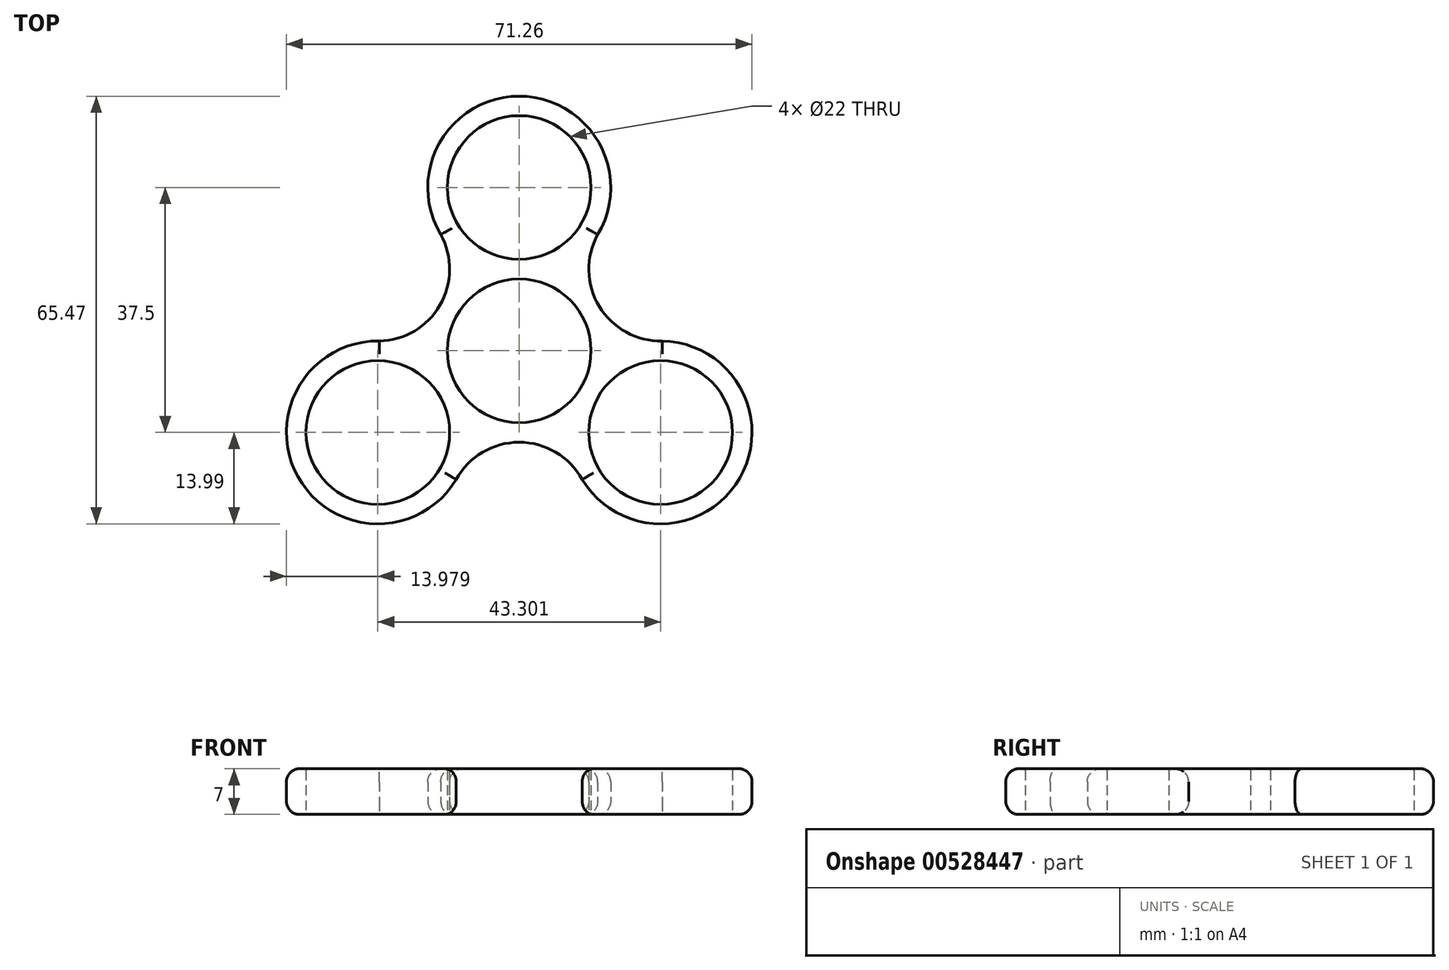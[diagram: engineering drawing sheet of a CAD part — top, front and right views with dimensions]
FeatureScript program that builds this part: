
annotation { "Feature Type Name" : "Feature", "Feature Type Description" : "" }
export const myFeature = defineFeature(function(context is Context, id is Id, definition is map)
    precondition{}
    {
        {
            var Q0;
            Q0=qCreatedBy(makeId("Top.planeOp"),FACE);
            var sketch = newSketch(context, id + "F0", { "sketchPlane" : qUnion([Q0])});
            skCircle(sketch, "E0", {"center": v(0, 0) * mm, "radius": 39 * mm, "construction": true});
            skCircle(sketch, "E1", {"center": v(0, 0) * mm, "radius": 11 * mm});
            skLineSegment(sketch, "E2", {"start": v(0, 39) * mm, "end": v(0, -39) * mm, "construction": true});
            skLineSegment(sketch, "E3", {"start": v(-39, 0) * mm, "end": v(39, 0) * mm, "construction": true});
            skCircle(sketch, "E4", {"center": v(0, 0) * mm, "radius": 25 * mm, "construction": true});
            skCircle(sketch, "E5", {"center": v(0, 25) * mm, "radius": 11 * mm});
            skCircle(sketch, "E6.1.0", {"center": v(-21.65, -12.5) * mm, "radius": 11 * mm});
            skCircle(sketch, "E6.2.0", {"center": v(21.65, -12.5) * mm, "radius": 11 * mm});
            skCircle(sketch, "E7", {"center": v(0, -25) * mm, "radius": 11 * mm, "construction": true});
            skCircle(sketch, "E8.1.0", {"center": v(21.65, 12.5) * mm, "radius": 11 * mm, "construction": true});
            skCircle(sketch, "E8.2.0", {"center": v(-21.65, 12.5) * mm, "radius": 11 * mm, "construction": true});
            skArc(sketch, "E9", {"start": v(-24.92, -2) * mm, "mid": v(-13.03, 7.52) * mm, "end": v(-10.73, 22.58) * mm, "construction": true});
            skArc(sketch, "E10.1.0", {"start": v(14.19, -20.58) * mm, "mid": v(0, -15.05) * mm, "end": v(-14.19, -20.58) * mm, "construction": true});
            skArc(sketch, "E10.2.0", {"start": v(10.73, 22.58) * mm, "mid": v(13.03, 7.52) * mm, "end": v(24.92, -2) * mm, "construction": true});
            skArc(sketch, "E11", {"start": v(-24.92, -2) * mm, "mid": v(-31.16, -18) * mm, "end": v(-14.19, -20.58) * mm, "construction": true});
            skArc(sketch, "E12", {"start": v(14.19, -20.58) * mm, "mid": v(31.16, -18) * mm, "end": v(24.92, -2) * mm, "construction": true});
            skArc(sketch, "E13", {"start": v(10.73, 22.58) * mm, "mid": v(0, 35.98) * mm, "end": v(-10.73, 22.58) * mm});
            skArc(sketch, "E14.2", {"start": v(-21.4, 1.5) * mm, "mid": v(-33.87, -19.28) * mm, "end": v(-9.64, -19.7) * mm});
            skArc(sketch, "E14.3", {"start": v(12, 17.79) * mm, "mid": v(0, 38.98) * mm, "end": v(-12, 17.79) * mm});
            skArc(sketch, "E14.5", {"start": v(9.4, -19.3) * mm, "mid": v(33.64, -19.7) * mm, "end": v(21.88, 1.5) * mm});
            skArc(sketch, "E15", {"start": v(-21.4, 1.5) * mm, "mid": v(-12.12, 7) * mm, "end": v(-12, 17.79) * mm});
            skArc(sketch, "E16", {"start": v(-9.64, -19.7) * mm, "mid": v(0, -14) * mm, "end": v(9.64, -19.7) * mm});
            skArc(sketch, "E17", {"start": v(21.88, 1.5) * mm, "mid": v(12.25, 6.8) * mm, "end": v(12, 17.79) * mm});
            skSolve(sketch);
        }
        {
            var Q0;
            Q0=makeQuery(id+"F0.imprint","IMPRINT",FACE,{"disambiguationData":[TD([[makeQuery(id+"F0.imprint","IMPRINT",EDGE,{"derivedFrom":sQuery(id+"F0.wireOp",EDGE,"E1")}),-1.0]])]});
            extrude(context, id + "F1", {"entities" : qUnion([Q0]), "depth" : 7 * mm, "offsetDistance" : 25 * mm});
        }
        {
            var Q0;
            Q0=makeQuery(id+"F1.opExtrude","CAP_EDGE",EDGE,{"disambiguationData":[OSD([sQuery(id+"F0.wireOp",EDGE,"E16")])],"isStart":false});
            var Q1;
            Q1=makeQuery(id+"F1.opExtrude","CAP_EDGE",EDGE,{"disambiguationData":[OSD([sQuery(id+"F0.wireOp",EDGE,"E14.2")])],"isStart":false});
            var Q2;
            Q2=makeQuery(id+"F1.opExtrude","CAP_EDGE",EDGE,{"disambiguationData":[OSD([sQuery(id+"F0.wireOp",EDGE,"E14.5")])],"isStart":false});
            var Q3;
            Q3=makeQuery(id+"F1.opExtrude","CAP_EDGE",EDGE,{"disambiguationData":[OSD([sQuery(id+"F0.wireOp",EDGE,"E17")])],"isStart":false});
            var Q4;
            Q4=makeQuery(id+"F1.opExtrude","CAP_EDGE",EDGE,{"disambiguationData":[OSD([sQuery(id+"F0.wireOp",EDGE,"E14.3")])],"isStart":false});
            var Q5;
            Q5=makeQuery(id+"F1.opExtrude","CAP_EDGE",EDGE,{"disambiguationData":[OSD([sQuery(id+"F0.wireOp",EDGE,"E14.3")])],"isStart":true});
            var Q6;
            Q6=makeQuery(id+"F1.opExtrude","CAP_EDGE",EDGE,{"disambiguationData":[OSD([sQuery(id+"F0.wireOp",EDGE,"E14.5")])],"isStart":true});
            var Q7;
            Q7=makeQuery(id+"F1.opExtrude","CAP_EDGE",EDGE,{"disambiguationData":[OSD([sQuery(id+"F0.wireOp",EDGE,"E16")])],"isStart":true});
            var Q8;
            Q8=makeQuery(id+"F1.opExtrude","CAP_EDGE",EDGE,{"disambiguationData":[OSD([sQuery(id+"F0.wireOp",EDGE,"E14.2")])],"isStart":true});
            fillet(context, id + "F2", {"entities" : qUnion([Q0, Q1, Q2, Q3, Q4, Q5, Q6, Q7, Q8]), "radius" : 2 * mm, "tangentPropagation" : true, "allowEdgeOverflow" : false});
        }
        {
            var Q0;
            Q0=makeQuery(id+"F1.opExtrude","CAP_EDGE",EDGE,{"disambiguationData":[OSD([sQuery(id+"F0.wireOp",EDGE,"E6.1.0")])],"isStart":false});
            var Q1;
            Q1=makeQuery(id+"F1.opExtrude","CAP_EDGE",EDGE,{"disambiguationData":[OSD([sQuery(id+"F0.wireOp",EDGE,"E1")])],"isStart":false});
            var Q2;
            Q2=makeQuery(id+"F1.opExtrude","CAP_EDGE",EDGE,{"disambiguationData":[OSD([sQuery(id+"F0.wireOp",EDGE,"E5")])],"isStart":false});
            var Q3;
            Q3=makeQuery(id+"F1.opExtrude","CAP_EDGE",EDGE,{"disambiguationData":[OSD([sQuery(id+"F0.wireOp",EDGE,"E6.2.0")])],"isStart":false});
            var Q4;
            Q4=makeQuery(id+"F1.opExtrude","CAP_EDGE",EDGE,{"disambiguationData":[OSD([sQuery(id+"F0.wireOp",EDGE,"E6.1.0")])],"isStart":true});
            var Q5;
            Q5=makeQuery(id+"F1.opExtrude","CAP_EDGE",EDGE,{"disambiguationData":[OSD([sQuery(id+"F0.wireOp",EDGE,"E6.2.0")])],"isStart":true});
            var Q6;
            Q6=makeQuery(id+"F1.opExtrude","CAP_EDGE",EDGE,{"disambiguationData":[OSD([sQuery(id+"F0.wireOp",EDGE,"E1")])],"isStart":true});
            var Q7;
            Q7=makeQuery(id+"F1.opExtrude","CAP_EDGE",EDGE,{"disambiguationData":[OSD([sQuery(id+"F0.wireOp",EDGE,"E5")])],"isStart":true});
            fillet(context, id + "F3", {"entities" : qUnion([Q0, Q1, Q2, Q3, Q4, Q5, Q6, Q7]), "radius" : .25 * mm, "tangentPropagation" : true, "allowEdgeOverflow" : false});
        }
    });
